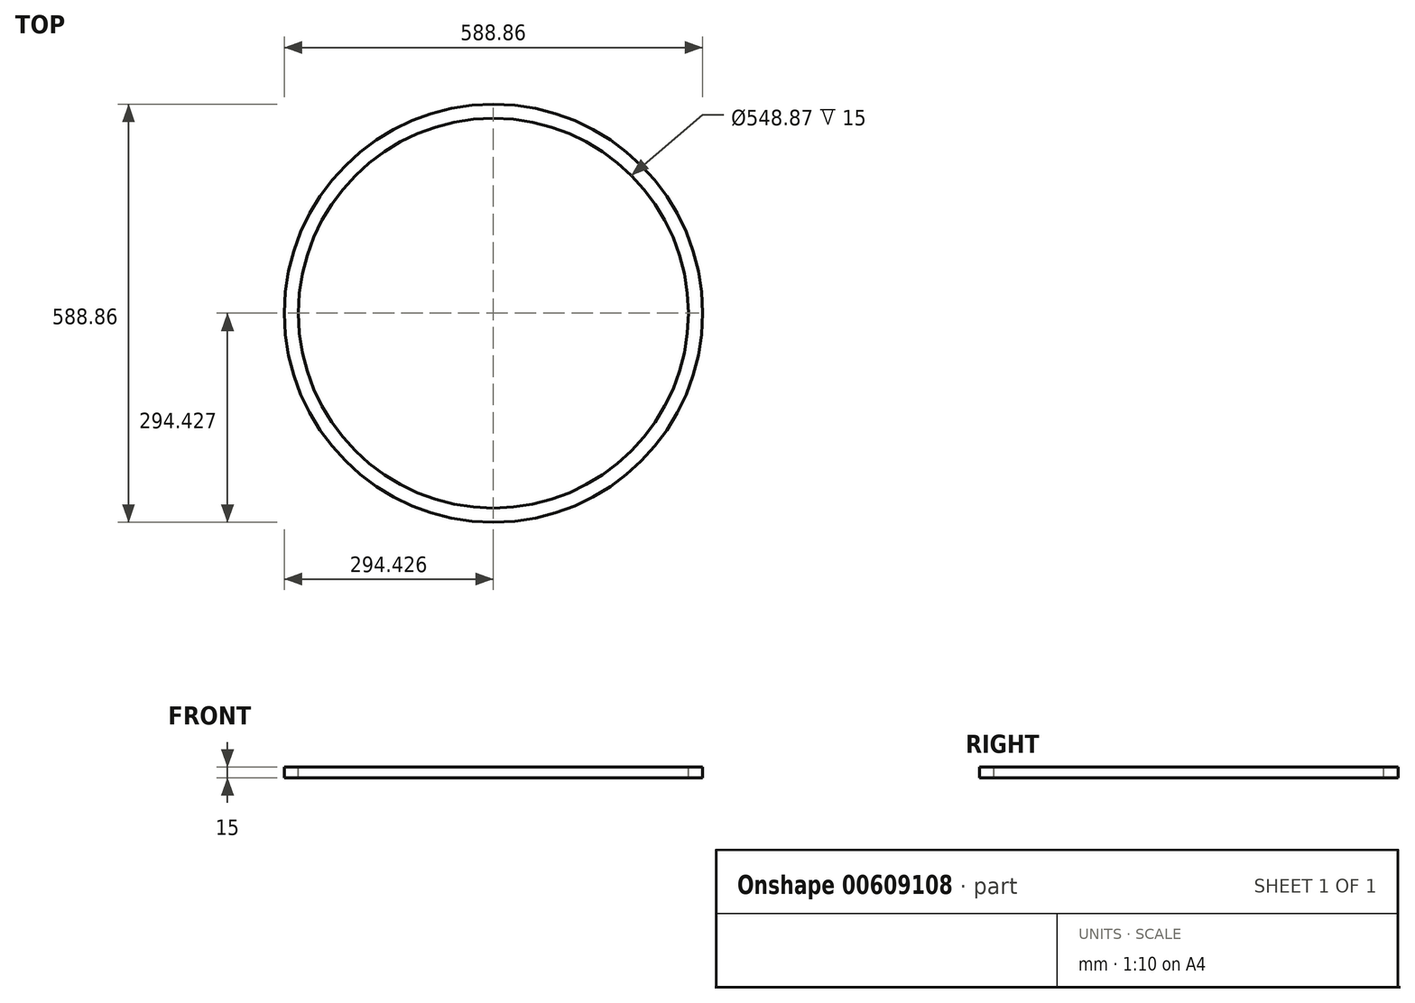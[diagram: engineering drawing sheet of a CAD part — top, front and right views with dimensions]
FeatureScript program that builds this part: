
annotation { "Feature Type Name" : "Feature", "Feature Type Description" : "" }
export const myFeature = defineFeature(function(context is Context, id is Id, definition is map)
    precondition{}
    {
        {
            var Q0;
            Q0=qCreatedBy(makeId("Front.planeOp"),FACE);
            var sketch = newSketch(context, id + "F0", { "sketchPlane" : qUnion([Q0])});
            skLineSegment(sketch, "E0.bottom", {"start": v(-10, 7.5) * mm, "end": v(10, 7.5) * mm});
            skLineSegment(sketch, "E0.top", {"start": v(-10, -7.5) * mm, "end": v(10, -7.5) * mm});
            skLineSegment(sketch, "E0.left", {"start": v(-10, 7.5) * mm, "end": v(-10, -7.5) * mm});
            skLineSegment(sketch, "E0.right", {"start": v(10, 7.5) * mm, "end": v(10, -7.5) * mm});
            skPoint(sketch, "E0.middle", {"position": v(0, 0) * mm});
            skSolve(sketch);
        }
        {
            var Q0;
            Q0=qCreatedBy(makeId("Top.planeOp"),FACE);
            var sketch = newSketch(context, id + "F1", { "sketchPlane" : qUnion([Q0])});
            skCircle(sketch, "E1", {"center": v(-284.4, -3.95) * mm, "radius": 284.43 * mm});
            skPoint(sketch, "E1.first.point", {"position": v(0, 0) * mm});
            skPoint(sketch, "E1.second.point", {"position": v(-568.35, -20.58) * mm});
            skPoint(sketch, "E1.third.point", {"position": v(-527.94, 143) * mm});
            skSolve(sketch);
        }
        {
            var Q0;
            Q0=makeQuery(id+"F0.imprint","IMPRINT",FACE,{"disambiguationData":[TD([[makeQuery(id+"F0.imprint","IMPRINT",EDGE,{"derivedFrom":sQuery(id+"F0.wireOp",EDGE,"E0.bottom")}),-1.0]])]});
            var Q1;
            Q1=sQuery(id+"F1.wireOp",EDGE,"E1");
            sweep(context, id + "F2", {"profiles" : qUnion([Q0]), "path" : qUnion([Q1])});
        }
    });
